# Revit family: equip-sink-elkay-sta-wall-ewma
name_source: partatom
category: Plumbing Fixtures
units: mm (PartAtom-declared; Revit-internal decimal feet)

## family parameters
Cut with Voids When Loaded = No
Host = Face
Part Type = Normal
Room Calculation Point = No
Round Connector Dimension = Use Radius
Shared = No

## types (8) — shared parameters
AC Power = No
Angle to Drain = 90.00°
Assembly Code = D2010410
Backsplash Height = 0' - 10"
Backsplash Width = 0' - 2"
Bowl Depth = 0' - 8"
Bowl Drain Location FB = 0' - 6 7/8"
Bowl Width = 1' - 1 3/4"
Bracket Front from Wall = 1' - 2"
Bubbler CW Flow Rate = 2 GPM
Bubbler Material = Metal - Steel - Stainless - Chrome
Bubbler Nominal Dia = 0' - 0 1/2"
Bubbler Nominal Radius = 0' - 0 1/4"
CW Flow Rate = 2 GPM
Cost = 1 $
Default Elevation = 3' - 0"
Description = Wash-Up Lavatory Sinks
Drain Material = Metal - Steel - Stainless - Chrome
Drain Pipe Extension = 0' - 1 11/16"
Faucet 1 Hole A Front = 0' - 0 1/4"
Faucet 4 Hole B Front = 0' - 0 1/4"
Faucet CL Vert to Bottom of Control Box Inlet = 2' - 2 11/32"
Faucet CL to AC Adapter = 0' - 7"
Faucet CL to AC Adapter Elev = 1' - 10"
Faucet CL to Top Backsplash = 0' - 4"
Faucet CL to Wall = 0' - 3"
Faucet Hole One = No
Faucet Hole Three = No
Faucet Hole Two = Yes
Faucet Material = Metal - Steel - Stainless - Chrome
Faucet Water Supply Radius = 0' - 0 3/16"
GN08 = No
HW Flow Rate = 2 GPM
Hidden Width = 1' - 8"
Keynote = D2010410
Manufacturer = Elkay Manufacturing
MasterFormat Number = 22.42.16.16
MasterFormat Title = Commercial Sinks
Mechanical Mix Valve = No
No Mix Valve = No
Nominal Dia = 0' - 0 1/2"
Nominal Radius = 0' - 0 1/4"
OmniClass Code = 23.45.05.14.14.27
OmniClass Title = Service Sinks
Rough-In Sanitary Installation Height = 1' - 11"
Rough-In Sanitary Right From CL Sink = 0' - 0"
Sanitary Flow Rate = 10 GPM
Sanitary Nominal Dia = 0' - 1 1/2"
Sanitary Nominal Radius = 0' - 0 3/4"
Side Splashes = No
Sink Bottom Corner From Front = 0' - 4 1/4"
Sink Material = Metal - Steel - Stainless - Chrome
Sink Rim Front Width = 0' - 1 1/2"
Sink Rim Left Width = 0' - 1 1/2"
Sink Rim Right Width = 0' - 1 1/2"
Sink San Conn Extr Visibility = No
Sink Width = 1' - 8"
Specification Sheet URL = http://www.elkayusa.com
Stem Material = Metal - Steel
Supply Line Mix Length = 0' - 0 1/2"
T4 = No
Thermostatic Mix Valve = No
URL = www.elkayusa.com
Valve Material = Metal - Brass
Vent Connection = Yes
zero-valued in all types: CWFU, HWFU, WFU

## per-type parameters (varying)
- EWMA60203: Bowl Length=4' - 8 1/2"; Drain CL LR to Left Bowl Edge=2' - 4 1/4"; Faucet 1 Hole A to B=0' - 2"; Faucet 1 Hole A to Faucet 1 CL=0' - 0 1/32"; Faucet 1 Hole A to Rough-In Water Supply CL 1=0' - 0"; Faucet 1 Hole B Front=0' - 0 1/8"; Faucet 2 Hole A From CL=0' - 0"; Faucet 2 Hole A Front=0' - 0 1/4"; Faucet 2 Hole A to Faucet 2 CL=0' - 0 1/32"; Faucet 2 Hole A to Rough-In Water Supply CL 2=0' - 0"; Faucet 2 Hole B Front=0' - 0 1/8"; Faucet 2 Hole B from Hole A=0' - 2"; Faucet 2 Rough-In Water Supply CL Separation=0' - 7"; Faucet 3 Hole A Front=0' - 0 1/8"; Faucet 3 Hole B Front=0' - 0 1/8"; Faucet 3 Hole B from CL=0' - 9"; Faucet 3 Hole B to A=0' - 2"; Faucet 3 Hole B to Faucet 3 CL=0' - 1"; Faucet 3 Hole B to Rough-In Water Supply CL 3=0' - 0 1/32"; Faucet 3 Rough-In Water Supply CL Separation=0' - 1 1/4"; Faucet 4 Hole A Front=0' - 0 1/8"; Faucet 4 Hole B to A=0' - 2"; Faucet 4 Hole B to Faucet 4 CL=0' - 0 1/32"; Faucet 4 Hole B to Rough-In Water Supply CL 4=0' - 0"; Faucet Hole Dia=0' - 1 1/2"; Hidden Length=5' - 0"; Hole Radius=0' - 0 3/4"; Model=EWMA60203; Rough-In Water Supply CL Separation=0' - 7"; Rough-In Water Supply Installation Height=0' - 8 5/8"; Sink Edge Left to Faucet 1 Hole A=0' - 10"; Sink Edge Right to Faucet 4 Hole B=0' - 10"; Sink Length=5' - 0"
- EWMA72203: Bowl Length=5' - 8 1/2"; Drain CL LR to Left Bowl Edge=2' - 10 1/4"; Faucet 1 Hole A to B=0' - 2"; Faucet 1 Hole A to Faucet 1 CL=0' - 0 1/32"; Faucet 1 Hole A to Rough-In Water Supply CL 1=0' - 0"; Faucet 1 Hole B Front=0' - 0 1/8"; Faucet 2 Hole A From CL=0' - 0"; Faucet 2 Hole A Front=0' - 0 1/4"; Faucet 2 Hole A to Faucet 2 CL=0' - 0 1/32"; Faucet 2 Hole A to Rough-In Water Supply CL 2=0' - 0"; Faucet 2 Hole B Front=0' - 0 1/8"; Faucet 2 Hole B from Hole A=0' - 2"; Faucet 2 Rough-In Water Supply CL Separation=0' - 7"; Faucet 3 Hole A Front=0' - 0 1/8"; Faucet 3 Hole B Front=0' - 0 1/8"; Faucet 3 Hole B from CL=0' - 9"; Faucet 3 Hole B to A=0' - 2"; Faucet 3 Hole B to Faucet 3 CL=0' - 1"; Faucet 3 Hole B to Rough-In Water Supply CL 3=0' - 0 1/32"; Faucet 3 Rough-In Water Supply CL Separation=0' - 1 1/4"; Faucet 4 Hole A Front=0' - 0 1/8"; Faucet 4 Hole B to A=0' - 2"; Faucet 4 Hole B to Faucet 4 CL=0' - 0 1/32"; Faucet 4 Hole B to Rough-In Water Supply CL 4=0' - 0"; Faucet Hole Dia=0' - 1 1/2"; Hidden Length=6' - 0"; Hole Radius=0' - 0 3/4"; Model=EWMA72203; Rough-In Water Supply CL Separation=0' - 7"; Rough-In Water Supply Installation Height=0' - 8 5/8"; Sink Edge Left to Faucet 1 Hole A=1' - 0"; Sink Edge Right to Faucet 4 Hole B=1' - 0"; Sink Length=6' - 0"
- EWMA48202: Bowl Length=3' - 8 1/2"; Drain CL LR to Left Bowl Edge=1' - 10 1/4"; Faucet 1 Hole A to B=0' - 2"; Faucet 1 Hole A to Faucet 1 CL=0' - 0 1/32"; Faucet 1 Hole A to Rough-In Water Supply CL 1=0' - 0"; Faucet 1 Hole B Front=0' - 0 1/8"; Faucet 2 Hole A From CL=0' - 6"; Faucet 2 Hole A Front=0' - 0 1/8"; Faucet 2 Hole A to Faucet 2 CL=0' - 1"; Faucet 2 Hole A to Rough-In Water Supply CL 2=0' - 0 1/32"; Faucet 2 Hole B Front=0' - 0 1/8"; Faucet 2 Hole B from Hole A=0' - 2"; Faucet 2 Rough-In Water Supply CL Separation=0' - 1 1/4"; Faucet 3 Hole A Front=0' - 0 1/8"; Faucet 3 Hole B Front=0' - 0 1/8"; Faucet 3 Hole B from CL=0' - 6"; Faucet 3 Hole B to A=0' - 2"; Faucet 3 Hole B to Faucet 3 CL=0' - 1"; Faucet 3 Hole B to Rough-In Water Supply CL 3=0' - 0 1/32"; Faucet 3 Rough-In Water Supply CL Separation=0' - 1 1/2"; Faucet 4 Hole A Front=0' - 0 1/8"; Faucet 4 Hole B to A=0' - 2"; Faucet 4 Hole B to Faucet 4 CL=0' - 0 1/32"; Faucet 4 Hole B to Rough-In Water Supply CL 4=0' - 0"; Faucet Hole Dia=0' - 1 1/4"; Hidden Length=4' - 0"; Hole Radius=0' - 0 5/8"; Model=EWMA48202; Rough-In Water Supply CL Separation=0' - 7"; Rough-In Water Supply Installation Height=0' - 8 5/8"; Sink Edge Left to Faucet 1 Hole A=1' - 0"; Sink Edge Right to Faucet 4 Hole B=1' - 0"; Sink Length=4' - 0"
- EWMA48204: Bowl Length=3' - 8 1/2"; Drain CL LR to Left Bowl Edge=1' - 10 1/4"; Faucet 1 Hole A to B=0' - 8"; Faucet 1 Hole A to Faucet 1 CL=0' - 4"; Faucet 1 Hole A to Rough-In Water Supply CL 1=0' - 4"; Faucet 1 Hole B Front=0' - 0 1/4"; Faucet 2 Hole A From CL=0' - 5"; Faucet 2 Hole A Front=0' - 0 1/8"; Faucet 2 Hole A to Faucet 2 CL=0' - 1"; Faucet 2 Hole A to Rough-In Water Supply CL 2=0' - 0 1/32"; Faucet 2 Hole B Front=0' - 0 1/8"; Faucet 2 Hole B from Hole A=0' - 2"; Faucet 2 Rough-In Water Supply CL Separation=0' - 1 1/4"; Faucet 3 Hole A Front=0' - 0 1/8"; Faucet 3 Hole B Front=0' - 0 1/8"; Faucet 3 Hole B from CL=0' - 5"; Faucet 3 Hole B to A=0' - 2"; Faucet 3 Hole B to Faucet 3 CL=0' - 1"; Faucet 3 Hole B to Rough-In Water Supply CL 3=0' - 0 1/32"; Faucet 3 Rough-In Water Supply CL Separation=0' - 1 1/4"; Faucet 4 Hole A Front=0' - 0 1/4"; Faucet 4 Hole B to A=0' - 8"; Faucet 4 Hole B to Faucet 4 CL=0' - 4"; Faucet 4 Hole B to Rough-In Water Supply CL 4=0' - 4"; Faucet Hole Dia=0' - 1 1/2"; Hidden Length=4' - 0"; Hole Radius=0' - 0 3/4"; Model=EWMA48204; Rough-In Water Supply CL Separation=0' - 8"; Rough-In Water Supply Installation Height=3' - 6"; Sink Edge Left to Faucet 1 Hole A=0' - 8"; Sink Edge Right to Faucet 4 Hole B=0' - 8"; Sink Length=4' - 0"
- EWMA60206: Bowl Length=4' - 8 1/2"; Drain CL LR to Left Bowl Edge=2' - 4 1/4"; Faucet 1 Hole A to B=0' - 8"; Faucet 1 Hole A to Faucet 1 CL=0' - 4"; Faucet 1 Hole A to Rough-In Water Supply CL 1=0' - 4"; Faucet 1 Hole B Front=0' - 0 1/4"; Faucet 2 Hole A From CL=0' - 4"; Faucet 2 Hole A Front=0' - 0 1/4"; Faucet 2 Hole A to Faucet 2 CL=0' - 4"; Faucet 2 Hole A to Rough-In Water Supply CL 2=0' - 4"; Faucet 2 Hole B Front=0' - 0 1/4"; Faucet 2 Hole B from Hole A=0' - 8"; Faucet 2 Rough-In Water Supply CL Separation=0' - 8"; Faucet 3 Hole A Front=0' - 0 1/8"; Faucet 3 Hole B Front=0' - 0 1/8"; Faucet 3 Hole B from CL=0' - 9"; Faucet 3 Hole B to A=0' - 2"; Faucet 3 Hole B to Faucet 3 CL=0' - 1"; Faucet 3 Hole B to Rough-In Water Supply CL 3=0' - 0 1/32"; Faucet 3 Rough-In Water Supply CL Separation=0' - 1 1/4"; Faucet 4 Hole A Front=0' - 0 1/4"; Faucet 4 Hole B to A=0' - 8"; Faucet 4 Hole B to Faucet 4 CL=0' - 4"; Faucet 4 Hole B to Rough-In Water Supply CL 4=0' - 4"; Faucet Hole Dia=0' - 1 1/2"; Hidden Length=5' - 0"; Hole Radius=0' - 0 3/4"; Model=EWMA60206"; Rough-In Water Supply CL Separation=0' - 8"; Rough-In Water Supply Installation Height=3' - 6"; Sink Edge Left to Faucet 1 Hole A=0' - 6"; Sink Edge Right to Faucet 4 Hole B=0' - 6"; Sink Length=5' - 0"
- EWMA72206: Bowl Length=5' - 8 1/2"; Drain CL LR to Left Bowl Edge=2' - 10 1/4"; Faucet 1 Hole A to B=0' - 8"; Faucet 1 Hole A to Faucet 1 CL=0' - 4"; Faucet 1 Hole A to Rough-In Water Supply CL 1=0' - 4"; Faucet 1 Hole B Front=0' - 0 1/4"; Faucet 2 Hole A From CL=0' - 4"; Faucet 2 Hole A Front=0' - 0 1/4"; Faucet 2 Hole A to Faucet 2 CL=0' - 4"; Faucet 2 Hole A to Rough-In Water Supply CL 2=0' - 4"; Faucet 2 Hole B Front=0' - 0 1/4"; Faucet 2 Hole B from Hole A=0' - 8"; Faucet 2 Rough-In Water Supply CL Separation=0' - 8"; Faucet 3 Hole A Front=0' - 0 1/8"; Faucet 3 Hole B Front=0' - 0 1/8"; Faucet 3 Hole B from CL=0' - 9"; Faucet 3 Hole B to A=0' - 2"; Faucet 3 Hole B to Faucet 3 CL=0' - 1"; Faucet 3 Hole B to Rough-In Water Supply CL 3=0' - 0 1/32"; Faucet 3 Rough-In Water Supply CL Separation=0' - 1 1/4"; Faucet 4 Hole A Front=0' - 0 1/4"; Faucet 4 Hole B to A=0' - 8"; Faucet 4 Hole B to Faucet 4 CL=0' - 4"; Faucet 4 Hole B to Rough-In Water Supply CL 4=0' - 4"; Faucet Hole Dia=0' - 1 1/2"; Hidden Length=6' - 0"; Hole Radius=0' - 0 3/4"; Model=EWMA72206"; Rough-In Water Supply CL Separation=0' - 8"; Rough-In Water Supply Installation Height=3' - 6"; Sink Edge Left to Faucet 1 Hole A=0' - 8"; Sink Edge Right to Faucet 4 Hole B=0' - 8"; Sink Length=6' - 0"
- EWMA96208: Bowl Length=7' - 8 1/2"; Drain CL LR to Left Bowl Edge=3' - 10 1/4"; Faucet 1 Hole A to B=0' - 8"; Faucet 1 Hole A to Faucet 1 CL=0' - 4"; Faucet 1 Hole A to Rough-In Water Supply CL 1=0' - 4"; Faucet 1 Hole B Front=0' - 0 1/4"; Faucet 2 Hole A From CL=1' - 4"; Faucet 2 Hole A Front=0' - 0 1/4"; Faucet 2 Hole A to Faucet 2 CL=0' - 8"; Faucet 2 Hole A to Rough-In Water Supply CL 2=0' - 4"; Faucet 2 Hole B Front=0' - 0 1/4"; Faucet 2 Hole B from Hole A=0' - 8"; Faucet 2 Rough-In Water Supply CL Separation=0' - 8"; Faucet 3 Hole A Front=0' - 0 1/4"; Faucet 3 Hole B Front=0' - 0 1/4"; Faucet 3 Hole B from CL=1' - 4"; Faucet 3 Hole B to A=0' - 8"; Faucet 3 Hole B to Faucet 3 CL=0' - 4"; Faucet 3 Hole B to Rough-In Water Supply CL 3=0' - 4"; Faucet 3 Rough-In Water Supply CL Separation=0' - 8"; Faucet 4 Hole A Front=0' - 0 1/4"; Faucet 4 Hole B to A=0' - 8"; Faucet 4 Hole B to Faucet 4 CL=0' - 4"; Faucet 4 Hole B to Rough-In Water Supply CL 4=0' - 4"; Faucet Hole Dia=0' - 1 1/2"; Hidden Length=8' - 0"; Hole Radius=0' - 0 3/4"; Model=EWMA96208; Rough-In Water Supply CL Separation=0' - 8"; Rough-In Water Supply Installation Height=3' - 6"; Sink Edge Left to Faucet 1 Hole A=0' - 8"; Sink Edge Right to Faucet 4 Hole B=0' - 8"; Sink Length=8' - 0"
- EWMA96204: Bowl Length=7' - 8 1/2"; Drain CL LR to Left Bowl Edge=3' - 10 1/4"; Faucet 1 Hole A to B=0' - 2"; Faucet 1 Hole A to Faucet 1 CL=0' - 0 1/32"; Faucet 1 Hole A to Rough-In Water Supply CL 1=0' - 0"; Faucet 1 Hole B Front=0' - 0 1/8"; Faucet 2 Hole A From CL=1' - 0"; Faucet 2 Hole A Front=0' - 0 1/4"; Faucet 2 Hole A to Faucet 2 CL=0' - 0 1/32"; Faucet 2 Hole A to Rough-In Water Supply CL 2=0' - 0"; Faucet 2 Hole B Front=0' - 0 1/8"; Faucet 2 Hole B from Hole A=0' - 2"; Faucet 2 Rough-In Water Supply CL Separation=0' - 7"; Faucet 3 Hole A Front=0' - 0 1/8"; Faucet 3 Hole B Front=0' - 0 1/4"; Faucet 3 Hole B from CL=1' - 0"; Faucet 3 Hole B to A=0' - 2"; Faucet 3 Hole B to Faucet 3 CL=0' - 0 1/32"; Faucet 3 Hole B to Rough-In Water Supply CL 3=0' - 0"; Faucet 3 Rough-In Water Supply CL Separation=0' - 7"; Faucet 4 Hole A Front=0' - 0 1/8"; Faucet 4 Hole B to A=0' - 2"; Faucet 4 Hole B to Faucet 4 CL=0' - 0 1/32"; Faucet 4 Hole B to Rough-In Water Supply CL 4=0' - 0"; Faucet Hole Dia=0' - 1 1/2"; Hidden Length=8' - 0"; Hole Radius=0' - 0 3/4"; Model=EWMA96204; Rough-In Water Supply CL Separation=0' - 7"; Rough-In Water Supply Installation Height=0' - 8 5/8"; Sink Edge Left to Faucet 1 Hole A=1' - 0"; Sink Edge Right to Faucet 4 Hole B=1' - 0"; Sink Length=8' - 0"

note: column(s) folded — value = type name in every type: Sink Part

## geometry (parser evidence)
native form markers: Sweep x8
no freeform markers — native parametric forms only
